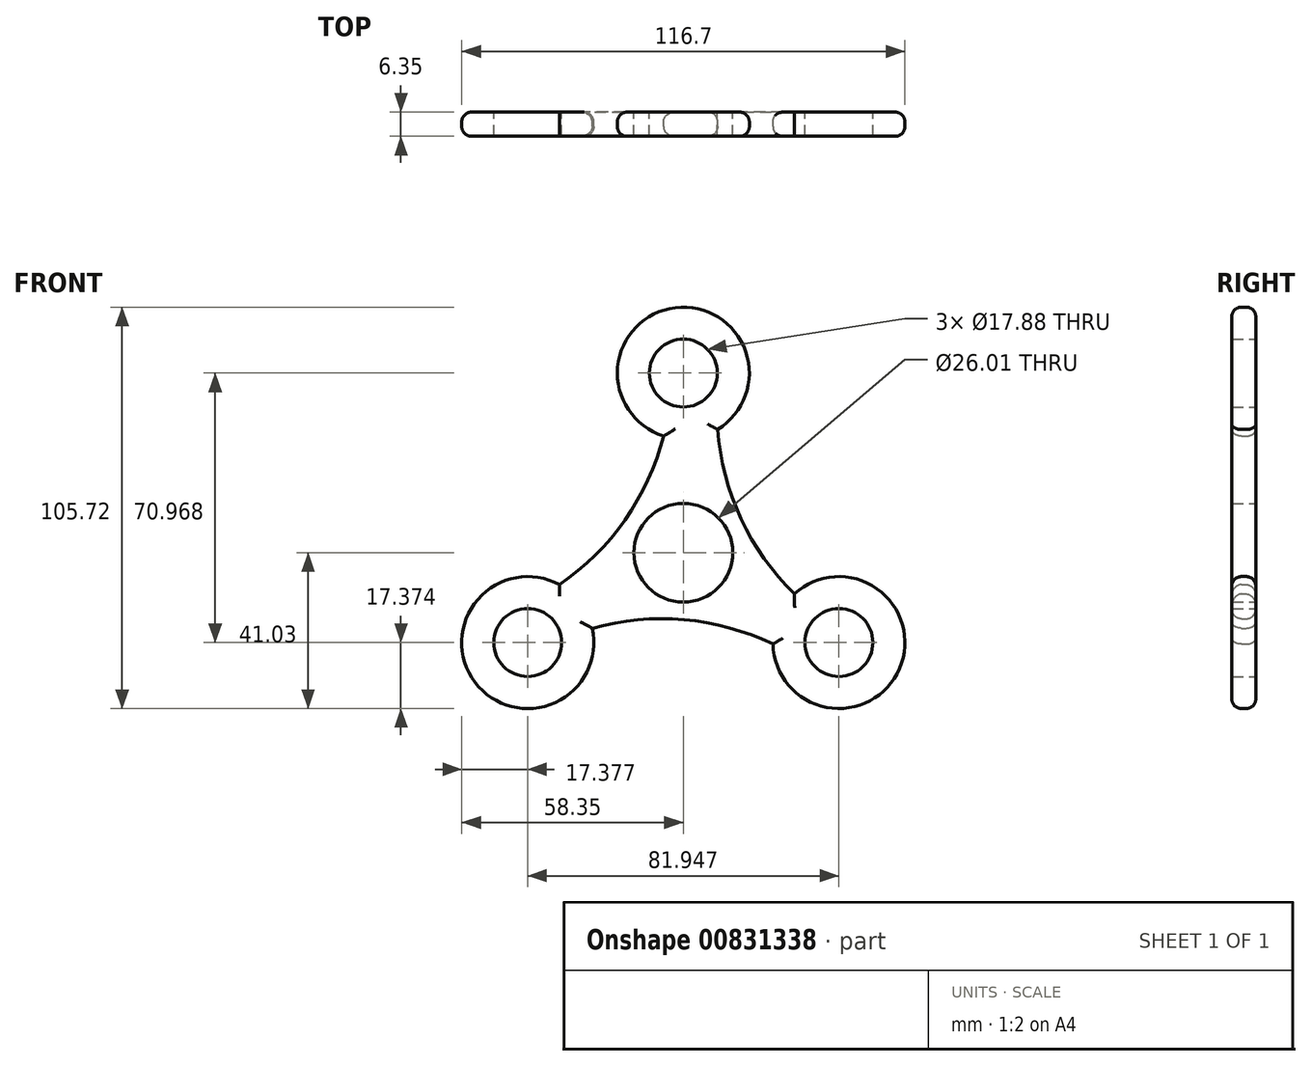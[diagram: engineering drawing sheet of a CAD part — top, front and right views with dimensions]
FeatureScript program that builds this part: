
annotation { "Feature Type Name" : "Feature", "Feature Type Description" : "" }
export const myFeature = defineFeature(function(context is Context, id is Id, definition is map)
    precondition{}
    {
        {
            var Q0;
            Q0=qCreatedBy(makeId("Front.planeOp"),FACE);
            var sketch = newSketch(context, id + "F0", { "sketchPlane" : qUnion([Q0])});
            skCircle(sketch, "E0", {"center": v(0, 0) * mm, "radius": 13 * mm});
            skArc(sketch, "E1", {"start": v(9.04, 32.47) * mm, "mid": v(-2.1, 64.56) * mm, "end": v(-5.21, 30.73) * mm});
            skCircle(sketch, "E2", {"center": v(0, 47.31) * mm, "radius": 8.94 * mm});
            skArc(sketch, "E3", {"start": v(9.04, 32.47) * mm, "mid": v(15.19, 8.97) * mm, "end": v(29.22, -10.85) * mm});
            skCircle(sketch, "E4.1.0", {"center": v(-40.97, -23.66) * mm, "radius": 8.94 * mm});
            skArc(sketch, "E4.1.1", {"start": v(-32.64, -8.4) * mm, "mid": v(-54.86, -34.1) * mm, "end": v(-24.01, -19.88) * mm});
            skArc(sketch, "E4.1.3", {"start": v(-32.64, -8.4) * mm, "mid": v(-15.36, 8.67) * mm, "end": v(-5.21, 30.73) * mm});
            skCircle(sketch, "E4.2.0", {"center": v(40.97, -23.66) * mm, "radius": 8.94 * mm});
            skArc(sketch, "E4.2.1", {"start": v(23.6, -24.06) * mm, "mid": v(56.96, -30.46) * mm, "end": v(29.22, -10.85) * mm});
            skArc(sketch, "E4.2.3", {"start": v(23.6, -24.06) * mm, "mid": v(0.18, -17.64) * mm, "end": v(-24.01, -19.88) * mm});
            skArc(sketch, "E5.trimOffspring", {"start": v(-3.61, 39.13) * mm, "mid": v(-3.57, 39.45) * mm, "end": v(-3.54, 39.76) * mm});
            skArc(sketch, "E6.trimOffspring", {"start": v(-32.09, -22.7) * mm, "mid": v(-32.38, -22.82) * mm, "end": v(-32.67, -22.94) * mm});
            skArc(sketch, "E7.trimOffspring", {"start": v(35.7, -16.44) * mm, "mid": v(35.95, -16.63) * mm, "end": v(36.2, -16.82) * mm});
            skSolve(sketch);
        }
        {
            var Q0;
            Q0 = qSketchRegion(id + "F0", true);
            extrude(context, id + "F1", {"entities" : qUnion([Q0]), "depth" : 6.35 * mm, "offsetDistance" : 25.4 * mm});
        }
        {
            var Q0;
            Q0=makeQuery(id+"F1.opExtrude","CAP_EDGE",EDGE,{"disambiguationData":[OSD([sQuery(id+"F0.wireOp",EDGE,"E4.1.1")])],"isStart":true});
            var Q1;
            Q1=makeQuery(id+"F1.opExtrude","CAP_EDGE",EDGE,{"disambiguationData":[OSD([sQuery(id+"F0.wireOp",EDGE,"E4.2.3")])],"isStart":true});
            var Q2;
            Q2=makeQuery(id+"F1.opExtrude","CAP_EDGE",EDGE,{"disambiguationData":[OSD([sQuery(id+"F0.wireOp",EDGE,"E4.2.1")])],"isStart":true});
            var Q3;
            Q3=makeQuery(id+"F1.opExtrude","CAP_EDGE",EDGE,{"disambiguationData":[OSD([sQuery(id+"F0.wireOp",EDGE,"E3")])],"isStart":true});
            var Q4;
            Q4=makeQuery(id+"F1.opExtrude","CAP_EDGE",EDGE,{"disambiguationData":[OSD([sQuery(id+"F0.wireOp",EDGE,"E4.1.3")])],"isStart":true});
            var Q5;
            Q5=makeQuery(id+"F1.opExtrude","CAP_EDGE",EDGE,{"disambiguationData":[OSD([sQuery(id+"F0.wireOp",EDGE,"E1")])],"isStart":true});
            fillet(context, id + "F2", {"entities" : qUnion([Q0, Q1, Q2, Q3, Q4, Q5]), "radius" : 2.54 * mm, "tangentPropagation" : true, "allowEdgeOverflow" : false});
        }
        {
            var Q0;
            Q0=makeQuery(id+"F1.opExtrude","CAP_EDGE",EDGE,{"disambiguationData":[OSD([sQuery(id+"F0.wireOp",EDGE,"E1")])],"isStart":false});
            var Q1;
            Q1=makeQuery(id+"F1.opExtrude","CAP_EDGE",EDGE,{"disambiguationData":[OSD([sQuery(id+"F0.wireOp",EDGE,"E3")])],"isStart":false});
            var Q2;
            Q2=makeQuery(id+"F1.opExtrude","CAP_EDGE",EDGE,{"disambiguationData":[OSD([sQuery(id+"F0.wireOp",EDGE,"E4.2.1")])],"isStart":false});
            var Q3;
            Q3=makeQuery(id+"F1.opExtrude","CAP_EDGE",EDGE,{"disambiguationData":[OSD([sQuery(id+"F0.wireOp",EDGE,"E4.2.3")])],"isStart":false});
            var Q4;
            Q4=makeQuery(id+"F1.opExtrude","CAP_EDGE",EDGE,{"disambiguationData":[OSD([sQuery(id+"F0.wireOp",EDGE,"E4.1.1")])],"isStart":false});
            var Q5;
            Q5=makeQuery(id+"F1.opExtrude","CAP_EDGE",EDGE,{"disambiguationData":[OSD([sQuery(id+"F0.wireOp",EDGE,"E4.1.3")])],"isStart":false});
            fillet(context, id + "F3", {"entities" : qUnion([Q0, Q1, Q2, Q3, Q4, Q5]), "radius" : 2.54 * mm, "tangentPropagation" : true, "allowEdgeOverflow" : false});
        }
    });
